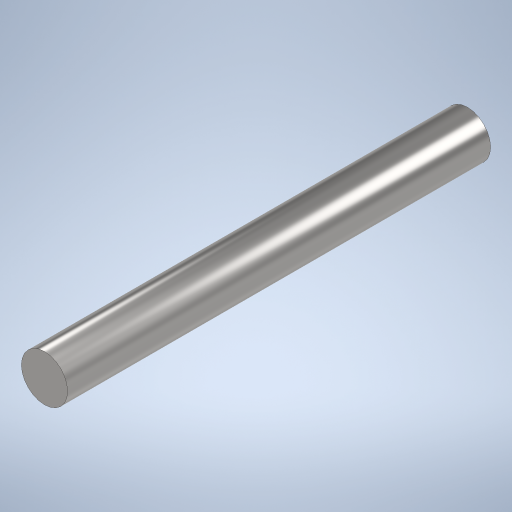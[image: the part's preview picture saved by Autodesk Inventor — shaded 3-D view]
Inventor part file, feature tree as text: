
AUTODESK INVENTOR PART (.ipt)
format: ipt  version: 2023 (Build 270158030, 158C)  size: 285,696 bytes
history: mixed  units: in
note: dims shown in document units (in); Inventor stores cm internally (conversion verified against a paired STEP export)
features: extrude x2, sketch x2, chamfer x1, imported_body x1
ambient origin geometry x8: Origin, YZ Plane, XZ Plane, XY Plane, X Axis, Y Axis, Z Axis, Center Point
bodies: Solid1 (imported_parasolid)
feature tree (6):
  extrude  "Extrusion1"  Depth=0.3937in TaperAngle=0.0deg
  extrude  "Extrusion2"  [1 undecoded]
  sketch  "Sketch1"  dims[d0=5.9055in d1=0.3937in d2=0.0in]
  sketch  "Sketch3"  dims[d3=2.3008in d4=0.0in]
  chamfer  "Chamfer1"  [1 undecoded]
  imported_body  NMx_Import_Brep_tag  [imported B-rep: ~3 faces, bbox_mm=[5.0, 5.0, 91.56]]
note: 2 required parameter values undecoded (feature->parameter linkage not recoverable at this tier; creation-order binding heuristic only, values carry confidence <= 0.55)
